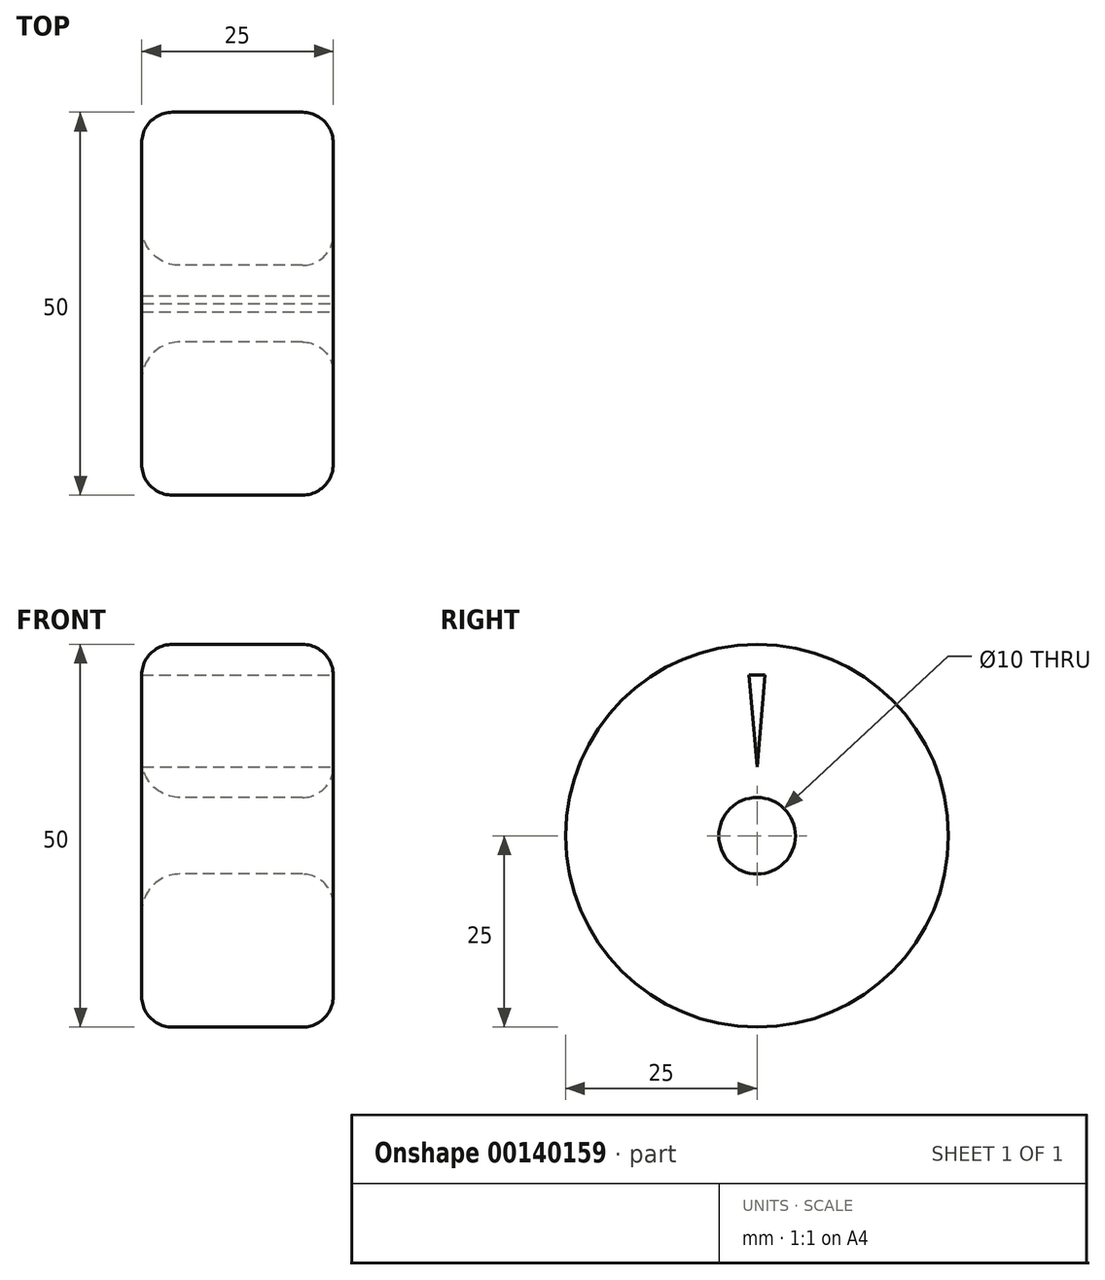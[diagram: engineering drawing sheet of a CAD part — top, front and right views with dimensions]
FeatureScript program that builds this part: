
annotation { "Feature Type Name" : "Feature", "Feature Type Description" : "" }
export const myFeature = defineFeature(function(context is Context, id is Id, definition is map)
    precondition{}
    {
        {
            var Q0;
            Q0=qCreatedBy(makeId("Right.planeOp"),FACE);
            var sketch = newSketch(context, id + "F0", { "sketchPlane" : qUnion([Q0])});
            skCircle(sketch, "E0", {"center": v(0, 0) * mm, "radius": 5 * mm});
            skCircle(sketch, "E1", {"center": v(0, 0) * mm, "radius": 25 * mm});
            skCircle(sketch, "E2", {"center": v(0, 0) * mm, "radius": 10 * mm});
            skSolve(sketch);
        }
        {
            var Q0;
            Q0=makeQuery(id+"F0.imprint","IMPRINT",FACE,{"disambiguationData":[TD([[makeQuery(id+"F0.imprint","IMPRINT",EDGE,{"derivedFrom":sQuery(id+"F0.wireOp",EDGE,"E0")}),-1.0]])]});
            extrude(context, id + "F1", {"entities" : qUnion([Q0]), "endBound" : BoundingType.SYMMETRIC, "depth" : 25 * mm});
        }
        {
            var Q0;
            Q0=makeQuery(id+"F0.imprint","IMPRINT",FACE,{"disambiguationData":[TD([[makeQuery(id+"F0.imprint","IMPRINT",EDGE,{"derivedFrom":sQuery(id+"F0.wireOp",EDGE,"E1")}),1.0]])]});
            extrude(context, id + "F2", {"entities" : qUnion([Q0]), "operationType" : NewBodyOperationType.ADD, "endBound" : BoundingType.SYMMETRIC, "depth" : 25 * mm});
        }
        {
            var Q0;
            Q0=makeQuery(id+"F1.opExtrude","CAP_EDGE",EDGE,{"disambiguationData":[OSD([sQuery(id+"F0.wireOp",EDGE,"E0")])],"isStart":true});
            fillet(context, id + "F3", {"entities" : qUnion([Q0]), "radius" : 5 * mm, "tangentPropagation" : true, "allowEdgeOverflow" : false});
        }
        {
            var Q0;
            Q0=makeQuery(id+"F2.opExtrude","CAP_EDGE",EDGE,{"disambiguationData":[OSD([sQuery(id+"F0.wireOp",EDGE,"E1")])],"isStart":false});
            var Q1;
            Q1=makeQuery(id+"F2.opExtrude","CAP_EDGE",EDGE,{"disambiguationData":[OSD([sQuery(id+"F0.wireOp",EDGE,"E1")])],"isStart":true});
            var Q2;
            Q2=makeQuery(id+"F1.opExtrude","CAP_EDGE",EDGE,{"disambiguationData":[OSD([sQuery(id+"F0.wireOp",EDGE,"E0")])],"isStart":false});
            fillet(context, id + "F4", {"entities" : qUnion([Q0, Q1, Q2]), "radius" : 4 * mm, "tangentPropagation" : true, "allowEdgeOverflow" : false});
        }
        {
            var Q0;
            {var subQ0=sQuery(id+"F0.wireOp",EDGE,"E2");Q0=makeQuery(id+"F2.boolean.opBoolean","MERGE",FACE,{"derivedFrom":[makeQuery(id+"F1.opExtrude","CAP_FACE",FACE,{"disambiguationData":[OSD([sQuery(id+"F0.wireOp",EDGE,"E0"),subQ0])],"isStart":false}),makeQuery(id+"F2.opExtrude","CAP_FACE",FACE,{"disambiguationData":[OSD([sQuery(id+"F0.wireOp",EDGE,"E1"),subQ0])],"isStart":false})]});}
            var sketch = newSketch(context, id + "F5", { "sketchPlane" : qUnion([Q0])});
            skLineSegment(sketch, "E3", {"start": v(0, 9) * mm, "end": v(1.05, 20.97) * mm});
            skLineSegment(sketch, "E4", {"start": v(0, 9) * mm, "end": v(-1.05, 20.97) * mm});
            skArc(sketch, "E5", {"start": v(1.05, 20.97) * mm, "mid": v(0, 21) * mm, "end": v(-1.05, 20.97) * mm});
            skSolve(sketch);
        }
        {
            var Q0;
            Q0 = qSketchRegion(id + "F5", true);
            extrude(context, id + "F6", {"entities" : qUnion([Q0]), "operationType" : NewBodyOperationType.REMOVE, "endBound" : BoundingType.THROUGH_ALL, "oppositeDirection" : true, "depth" : 25 * mm});
        }
    });
